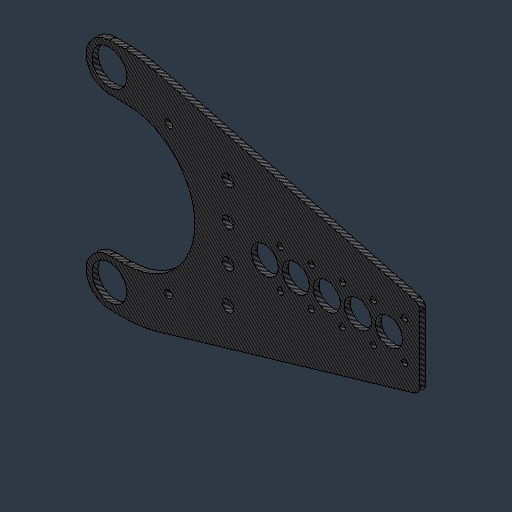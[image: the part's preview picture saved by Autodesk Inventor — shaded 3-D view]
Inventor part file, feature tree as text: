
AUTODESK INVENTOR PART (.ipt)
format: ipt  version: 2024.3 (Build 283343000, 343)  size: 325,120 bytes
history: native  units: mm (DEFAULTED — no unit token found)
features: sketch x6, hole x5, other x3, pattern_linear x2, chamfer x2, sheet_metal_op x1, mirror x1
ambient origin geometry x8: Origin, YZ Plane, XZ Plane, XY Plane, X Axis, Y Axis, Z Axis, Center Point
bodies: Solid1 (feature_tree)
feature tree (20):
  sheet_metal_op  "Face1"
  hole  "Hole1"  [1 undecoded]
  pattern_linear  "Rectangular Pattern1"  Count1=5 Spacing1=25.4mm
  sketch  "Sketch4"  dims[d7=31.75mm]
  hole  "Hole2"  [1 undecoded]
  hole  "Hole3"  [1 undecoded]
  sketch  "Sketch5"  dims[d8=12.7mm]
  hole  "Hole4"  [1 undecoded]
  pattern_linear  "Rectangular Pattern2"  Spacing1=44.45mm  [1 undecoded]
  chamfer  "Corner Round1"
  mirror  "Mirror2"
  hole  "Hole5"  [1 undecoded]
  chamfer  "Corner Round3"
  sketch  "Sketch2"  dims[d0=114.3mm d1=63.5mm]
  other  "Plate1"
  sketch  "Sketch3"  dims[d6=4.7625mm]
  sketch  "Sketch6"  dims[d9=5.1054mm d10=9.652mm d11=9.779mm d12=1.9558mm d13=14.3117mm d14=4.7625mm]
  sketch  "Sketch7"  dims[d15=20.594885mm d16=50.0mm d18=25.4mm d20=12.7mm d21=19.05mm d22=28.575mm d23=19.05mm d24=9.525mm d25=6.35mm d26=14.3117mm d27=25.4mm d28=20.594885mm d29=101.99878mm d30=44.45mm d31=9.525mm d32=19.05mm d33=9.525mm d34=6.35mm d35=14.3117mm d36=25.4mm d37=20.594885mm d38=22.86mm d39=29.633333mm d40=29.633333mm d41=29.633333mm d42=12.7mm d43=12.7mm d44=25.4mm d45=8.726646mm d47=33.3375mm d48=92.075mm d49=4.7625mm d50=0.0mm d51=6.35mm d52=22.225mm d53=19.05mm d54=9.525mm d55=6.35mm d56=14.3117mm d57=25.4mm d58=20.594885mm d59=50.0mm d61=25.4mm d63=44.45mm d65=57.15mm d66=12.7mm d67=26.9875mm d68=4.7625mm d69=0.0mm d70=3.175mm d71=6.35mm d72=3.175mm d73=241.3mm d75=19.05mm d76=14.2875mm d77=14.2875mm d78=3.175mm d79=6.35mm d80=19.05mm d81=9.525mm d82=6.35mm d83=14.3117mm d84=4.7625mm d85=20.594885mm d86=25.499695mm d87=50.99939mm d88=25.499695mm d89=15.875mm]
  other  "Cut1"
  other  "Cut2"
note: 6 required parameter values undecoded (feature->parameter linkage not recoverable at this tier; creation-order binding heuristic only, values carry confidence <= 0.55)
